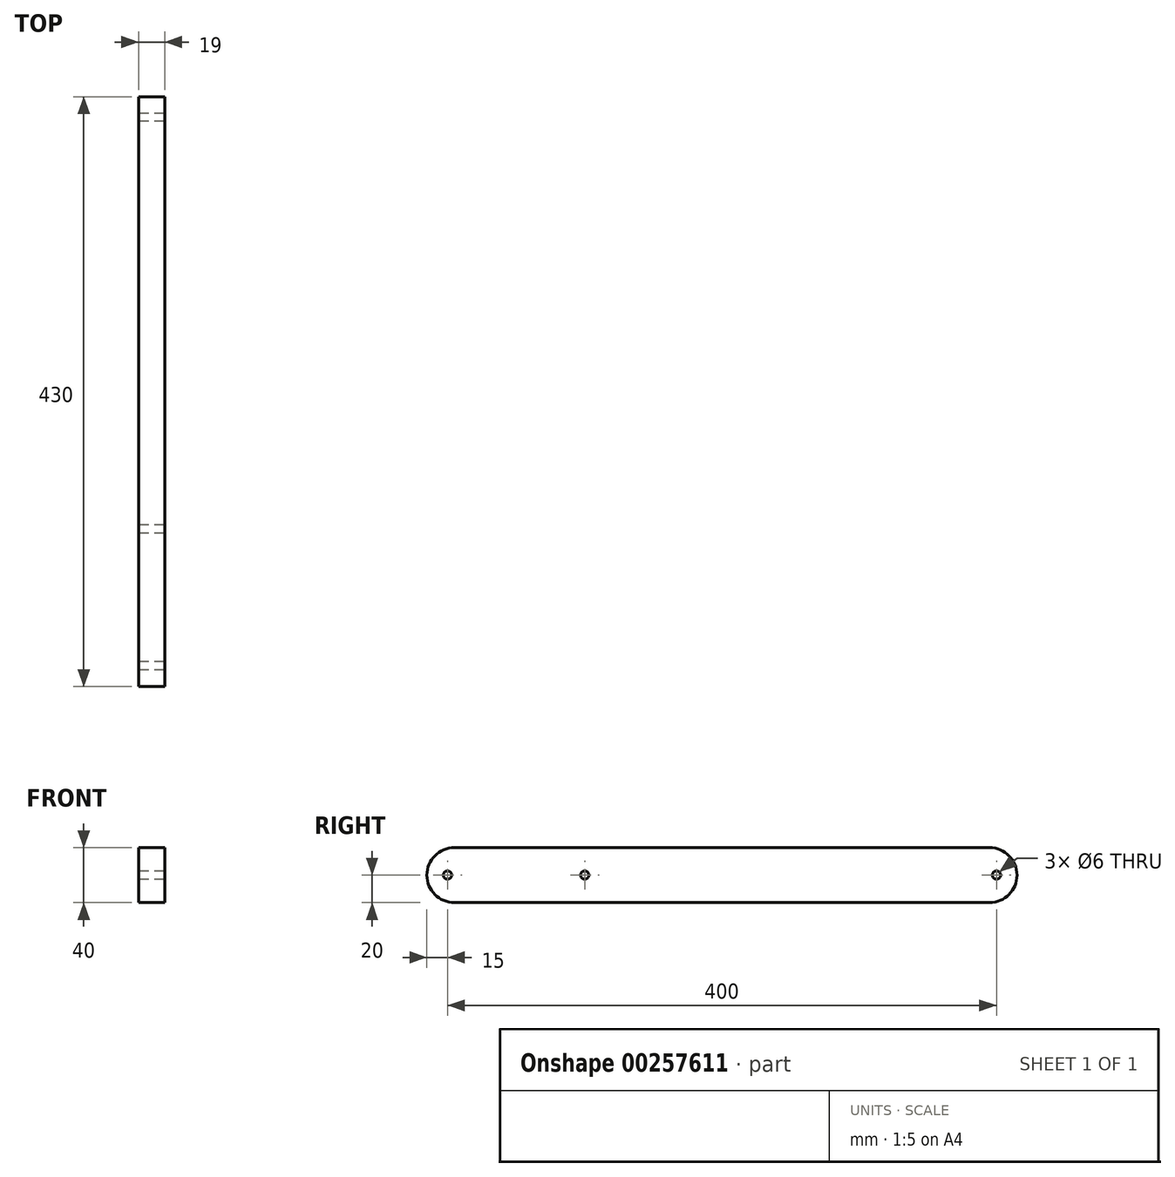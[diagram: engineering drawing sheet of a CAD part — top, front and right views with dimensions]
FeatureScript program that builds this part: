
annotation { "Feature Type Name" : "Feature", "Feature Type Description" : "" }
export const myFeature = defineFeature(function(context is Context, id is Id, definition is map)
    precondition{}
    {
        {
            var Q0;
            Q0=qCreatedBy(makeId("Right.planeOp"),FACE);
            var sketch = newSketch(context, id + "F0", { "sketchPlane" : qUnion([Q0])});
            skCircle(sketch, "E0", {"center": v(0, 0) * mm, "radius": 3 * mm});
            skCircle(sketch, "E1", {"center": v(-400, 0) * mm, "radius": 3 * mm});
            skLineSegment(sketch, "E2.bottom", {"start": v(-415, 20) * mm, "end": v(15, 20) * mm});
            skLineSegment(sketch, "E2.top", {"start": v(-415, -20) * mm, "end": v(15, -20) * mm});
            skLineSegment(sketch, "E2.left", {"start": v(-415, 20) * mm, "end": v(-415, -20) * mm});
            skLineSegment(sketch, "E2.right", {"start": v(15, 20) * mm, "end": v(15, -20) * mm});
            skSolve(sketch);
        }
        {
            var Q0;
            Q0=qSketchRegion(id+"F0",true);
            extrude(context, id + "F1", {"entities" : qUnion([Q0]), "depth" : 19 * mm});
        }
        {
            var Q0;
            Q0=makeQuery(id+"F1.opExtrude","SWEPT_EDGE",EDGE,{"disambiguationData":[OSD([sQuery(id+"F0.wireOp",EDGE,"E2.bottom"),sQuery(id+"F0.wireOp",EDGE,"E2.right")])]});
            var Q1;
            Q1=makeQuery(id+"F1.opExtrude","SWEPT_EDGE",EDGE,{"disambiguationData":[OSD([sQuery(id+"F0.wireOp",EDGE,"E2.top"),sQuery(id+"F0.wireOp",EDGE,"E2.right")])]});
            var Q2;
            Q2=makeQuery(id+"F1.opExtrude","SWEPT_EDGE",EDGE,{"disambiguationData":[OSD([sQuery(id+"F0.wireOp",EDGE,"E2.bottom"),sQuery(id+"F0.wireOp",EDGE,"E2.left")])]});
            var Q3;
            Q3=makeQuery(id+"F1.opExtrude","SWEPT_EDGE",EDGE,{"disambiguationData":[OSD([sQuery(id+"F0.wireOp",EDGE,"E2.top"),sQuery(id+"F0.wireOp",EDGE,"E2.left")])]});
            fillet(context, id + "F2", {"entities" : qUnion([Q0, Q1, Q2, Q3]), "radius" : 20 * mm, "tangentPropagation" : true, "allowEdgeOverflow" : false});
        }
        {
            var Q0;
            Q0=makeQuery(id+"F1.opExtrude","CAP_FACE",FACE,{"disambiguationData":[OSD([sQuery(id+"F0.wireOp",EDGE,"E0"),sQuery(id+"F0.wireOp",EDGE,"E1"),sQuery(id+"F0.wireOp",EDGE,"E2.bottom"),sQuery(id+"F0.wireOp",EDGE,"E2.top"),sQuery(id+"F0.wireOp",EDGE,"E2.left"),sQuery(id+"F0.wireOp",EDGE,"E2.right")])],"isStart":false});
            var sketch = newSketch(context, id + "F3", { "sketchPlane" : qUnion([Q0])});
            skCircle(sketch, "E3", {"center": v(-300, 0) * mm, "radius": 3 * mm});
            skSolve(sketch);
        }
        {
            var Q0;
            Q0 = qSketchRegion(id + "F3", true);
            extrude(context, id + "F4", {"entities" : qUnion([Q0]), "operationType" : NewBodyOperationType.REMOVE, "endBound" : BoundingType.THROUGH_ALL, "oppositeDirection" : true, "depth" : 25 * mm});
        }
    });
